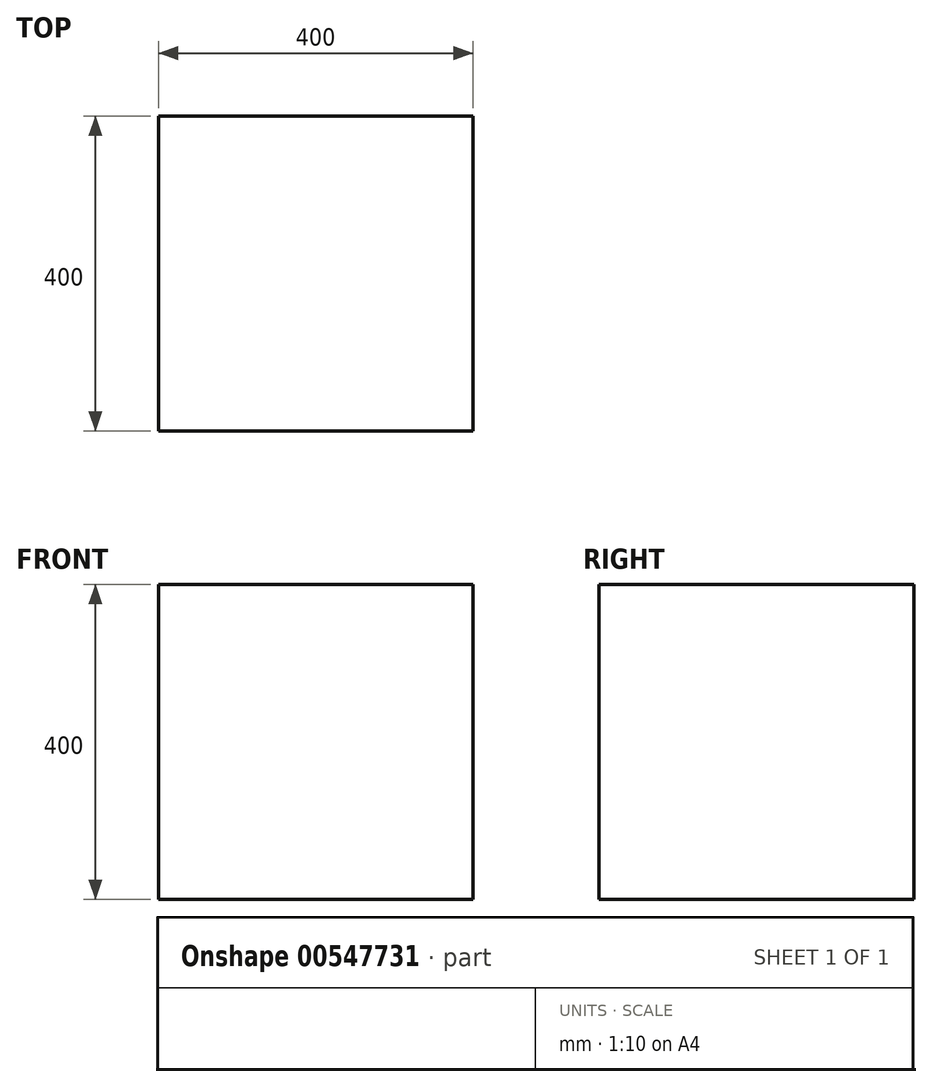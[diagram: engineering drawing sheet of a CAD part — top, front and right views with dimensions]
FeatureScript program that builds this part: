
annotation { "Feature Type Name" : "Feature", "Feature Type Description" : "" }
export const myFeature = defineFeature(function(context is Context, id is Id, definition is map)
    precondition{}
    {
        {
            var Q0;
            Q0=qCreatedBy(makeId("Top.planeOp"),FACE);
            var sketch = newSketch(context, id + "F0", { "sketchPlane" : qUnion([Q0])});
            skLineSegment(sketch, "E0.bottom", {"start": v(200, 200) * mm, "end": v(-200, 200) * mm});
            skLineSegment(sketch, "E0.top", {"start": v(200, -200) * mm, "end": v(-200, -200) * mm});
            skLineSegment(sketch, "E0.left", {"start": v(200, 200) * mm, "end": v(200, -200) * mm});
            skLineSegment(sketch, "E0.right", {"start": v(-200, 200) * mm, "end": v(-200, -200) * mm});
            skPoint(sketch, "E0.middle", {"position": v(0, 0) * mm});
            skSolve(sketch);
        }
        {
            var Q0;
            Q0 = qSketchRegion(id + "F0", true);
            extrude(context, id + "F1", {"entities" : qUnion([Q0]), "endBound" : BoundingType.SYMMETRIC, "depth" : 400 * mm, "offsetDistance" : 25 * mm});
        }
    });
